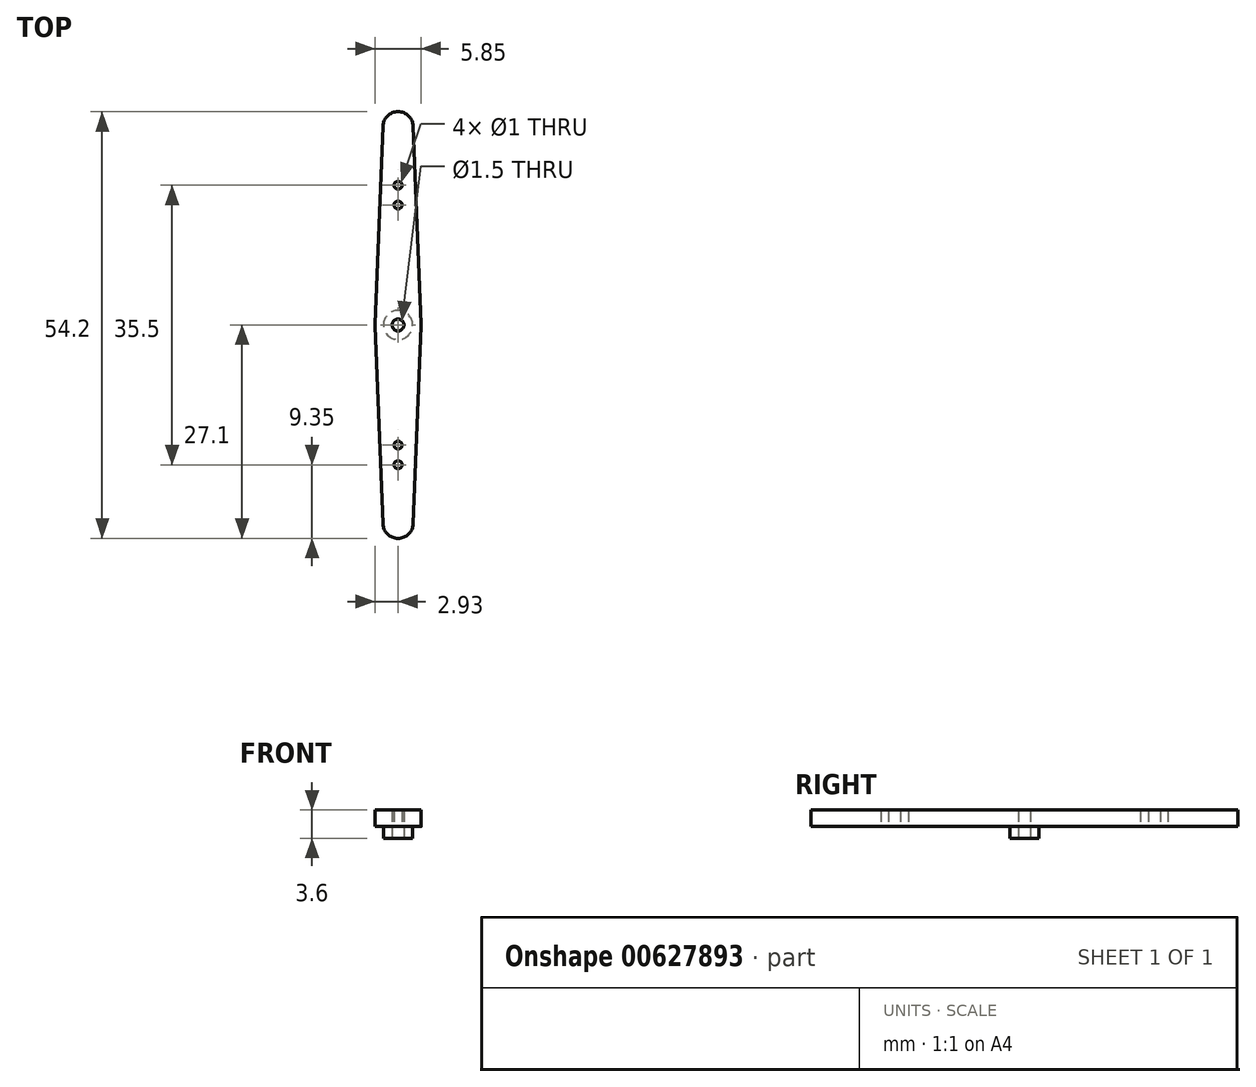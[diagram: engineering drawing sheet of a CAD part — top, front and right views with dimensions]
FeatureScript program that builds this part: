
annotation { "Feature Type Name" : "Feature", "Feature Type Description" : "" }
export const myFeature = defineFeature(function(context is Context, id is Id, definition is map)
    precondition{}
    {
        {
            var Q0;
            Q0=qCreatedBy(makeId("Top.planeOp"),FACE);
            var sketch = newSketch(context, id + "F0", { "sketchPlane" : qUnion([Q0])});
            skLineSegment(sketch, "E0", {"start": v(0, 0) * mm, "end": v(0, 24.29) * mm, "construction": true});
            skCircle(sketch, "E1", {"center": v(0, 0) * mm, "radius": 2.93 * mm});
            skCircle(sketch, "E2", {"center": v(0, 25.18) * mm, "radius": 1.93 * mm});
            skLineSegment(sketch, "E3", {"start": v(-1.92, 25.25) * mm, "end": v(-2.92, 0.12) * mm});
            skLineSegment(sketch, "E4", {"start": v(1.92, 25.25) * mm, "end": v(2.92, 0.12) * mm});
            skCircle(sketch, "E5", {"center": v(0, 0) * mm, "radius": 0.75 * mm});
            skLineSegment(sketch, "E6", {"start": v(0, 0) * mm, "end": v(15.2, 0) * mm, "construction": true});
            skCircle(sketch, "E7.MirrorC", {"center": v(0, -25.18) * mm, "radius": 1.93 * mm});
            skLineSegment(sketch, "E8", {"start": v(2.92, -0.12) * mm, "end": v(1.92, -25.25) * mm});
            skLineSegment(sketch, "E9", {"start": v(-2.92, -0.12) * mm, "end": v(-1.92, -25.25) * mm});
            skCircle(sketch, "E10", {"center": v(0, 15.25) * mm, "radius": 0.5 * mm});
            skCircle(sketch, "E11.MirrorC", {"center": v(0, -15.25) * mm, "radius": 0.5 * mm});
            skCircle(sketch, "E12", {"center": v(0, 17.75) * mm, "radius": 0.5 * mm});
            skCircle(sketch, "E13.MirrorC", {"center": v(0, -17.75) * mm, "radius": 0.5 * mm});
            skSolve(sketch);
        }
        {
            var Q0;
            Q0=qSketchRegion(id+"F0",true);
            extrude(context, id + "F1", {"entities" : qUnion([Q0]), "depth" : 2.1 * mm, "offsetDistance" : 25 * mm});
        }
        {
            var Q0;
            {var subQ0=sQuery(id+"F0.wireOp",EDGE,"E1");var subQ1=makeQuery(id+"F0.imprint","INTERSECT",VERTEX,{"derivedFrom":[subQ0,sQuery(id+"F0.wireOp",EDGE,"E3")]});Q0=makeQuery(id+"F0.imprint","IMPRINT",FACE,{"disambiguationData":[TD([[makeQuery(id+"F0.imprint","IMPRINT",EDGE,{"disambiguationData":[TD([[subQ1,1.0]])],"derivedFrom":subQ0}),1.0]])]});}
            var sketch = newSketch(context, id + "F2", { "sketchPlane" : qUnion([Q0])});
            skLineSegment(sketch, "E14.0.0", {"start": v(-2.92, 0.12) * mm, "end": v(-2.92, 0.12) * mm});
            skLineSegment(sketch, "E14.0.1", {"start": v(-2.92, 0.12) * mm, "end": v(-2.92, 0.12) * mm});
            skCircle(sketch, "E15", {"center": v(0, 0) * mm, "radius": 1.85 * mm});
            skCircle(sketch, "E16.0", {"center": v(0, 0) * mm, "radius": 0.75 * mm});
            skSolve(sketch);
        }
        {
            var Q0;
            Q0=qSketchRegion(id+"F2",true);
            extrude(context, id + "F3", {"entities" : qUnion([Q0]), "operationType" : NewBodyOperationType.ADD, "oppositeDirection" : true, "depth" : 1.5 * mm, "offsetDistance" : 25 * mm});
        }
    });
